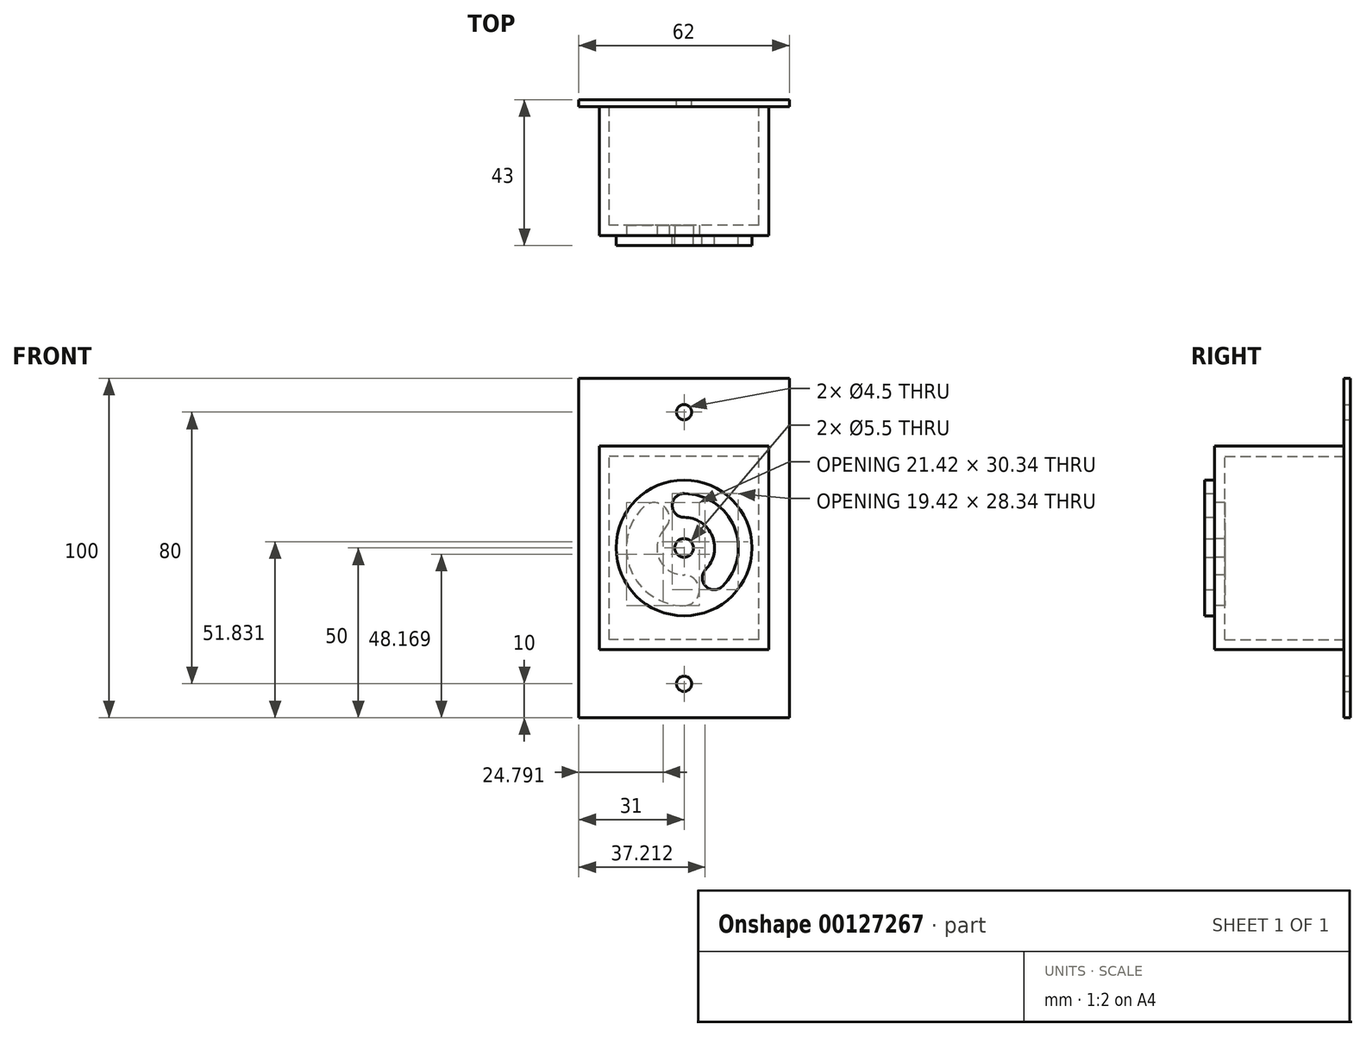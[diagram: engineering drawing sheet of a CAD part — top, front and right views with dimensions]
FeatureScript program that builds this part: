
annotation { "Feature Type Name" : "Feature", "Feature Type Description" : "" }
export const myFeature = defineFeature(function(context is Context, id is Id, definition is map)
    precondition{}
    {
        {
            var Q0;
            Q0=qCreatedBy(makeId("Front.planeOp"),FACE);
            var sketch = newSketch(context, id + "F0", { "sketchPlane" : qUnion([Q0])});
            skLineSegment(sketch, "E0.bottom", {"start": v(31, -50) * mm, "end": v(-31, -50) * mm});
            skLineSegment(sketch, "E0.top", {"start": v(31, 50) * mm, "end": v(-31, 50) * mm});
            skLineSegment(sketch, "E0.left", {"start": v(31, -50) * mm, "end": v(31, 50) * mm});
            skLineSegment(sketch, "E0.right", {"start": v(-31, -50) * mm, "end": v(-31, 50) * mm});
            skPoint(sketch, "E0.middle", {"position": v(0, 0) * mm});
            skCircle(sketch, "E1", {"center": v(0, 40) * mm, "radius": 2.25 * mm});
            skCircle(sketch, "E2.MirrorC", {"center": v(0, -40) * mm, "radius": 2.25 * mm});
            skSolve(sketch);
        }
        {
            var Q0;
            Q0=qSketchRegion(id+"F0",true);
            extrude(context, id + "F1", {"entities" : qUnion([Q0]), "depth" : 2 * mm});
        }
        {
            var Q0;
            Q0=makeQuery(id+"F1.opExtrude","CAP_FACE",FACE,{"disambiguationData":[OSD([sQuery(id+"F0.wireOp",EDGE,"E0.bottom"),sQuery(id+"F0.wireOp",EDGE,"E0.top"),sQuery(id+"F0.wireOp",EDGE,"E0.left"),sQuery(id+"F0.wireOp",EDGE,"E0.right"),sQuery(id+"F0.wireOp",EDGE,"E1"),sQuery(id+"F0.wireOp",EDGE,"E2.MirrorC")])],"isStart":false});
            var sketch = newSketch(context, id + "F2", { "sketchPlane" : qUnion([Q0])});
            skLineSegment(sketch, "E3.bottom", {"start": v(25, -30) * mm, "end": v(-25, -30) * mm});
            skLineSegment(sketch, "E3.top", {"start": v(25, 30) * mm, "end": v(-25, 30) * mm});
            skLineSegment(sketch, "E3.left", {"start": v(25, -30) * mm, "end": v(25, 30) * mm});
            skLineSegment(sketch, "E3.right", {"start": v(-25, -30) * mm, "end": v(-25, 30) * mm});
            skPoint(sketch, "E3.middle", {"position": v(0, 0) * mm});
            skLineSegment(sketch, "E4.0", {"start": v(-22, -27) * mm, "end": v(-22, 27) * mm});
            skLineSegment(sketch, "E4.1", {"start": v(22, -27) * mm, "end": v(-22, -27) * mm});
            skLineSegment(sketch, "E4.2", {"start": v(22, -27) * mm, "end": v(22, 27) * mm});
            skLineSegment(sketch, "E4.3", {"start": v(22, 27) * mm, "end": v(-22, 27) * mm});
            skSolve(sketch);
        }
        {
            var Q0;
            Q0=qSketchRegion(id+"F2",true);
            extrude(context, id + "F3", {"entities" : qUnion([Q0]), "operationType" : NewBodyOperationType.ADD, "depth" : 35 * mm});
        }
        {
            var Q0;
            Q0=makeQuery(id+"F3.boolean.opBoolean","SPLIT",FACE,{"disambiguationData":[TD([makeQuery(id+"F3.opExtrude","SWEPT_FACE",FACE,{"disambiguationData":[OSD([sQuery(id+"F2.wireOp",EDGE,"E4.0")])]})])],"derivedFrom":makeQuery(id+"F1.opExtrude","CAP_FACE",FACE,{"disambiguationData":[OSD([sQuery(id+"F0.wireOp",EDGE,"E0.bottom"),sQuery(id+"F0.wireOp",EDGE,"E0.top"),sQuery(id+"F0.wireOp",EDGE,"E0.left"),sQuery(id+"F0.wireOp",EDGE,"E0.right"),sQuery(id+"F0.wireOp",EDGE,"E1"),sQuery(id+"F0.wireOp",EDGE,"E2.MirrorC")])],"isStart":false})});
            extrude(context, id + "F4", {"entities" : qUnion([Q0]), "operationType" : NewBodyOperationType.REMOVE, "endBound" : BoundingType.THROUGH_ALL, "oppositeDirection" : true, "depth" : 25 * mm});
        }
        {
            var Q0;
            Q0=makeQuery(id+"F3.opExtrude","CAP_FACE",FACE,{"disambiguationData":[OSD([sQuery(id+"F2.wireOp",EDGE,"E3.bottom"),sQuery(id+"F2.wireOp",EDGE,"E3.top"),sQuery(id+"F2.wireOp",EDGE,"E3.left"),sQuery(id+"F2.wireOp",EDGE,"E3.right"),sQuery(id+"F2.wireOp",EDGE,"E4.0"),sQuery(id+"F2.wireOp",EDGE,"E4.1"),sQuery(id+"F2.wireOp",EDGE,"E4.2"),sQuery(id+"F2.wireOp",EDGE,"E4.3")])],"isStart":false});
            cPlane(context, id + "F5", {"entities" : qUnion([Q0]), "cplaneType" : CPlaneType.OFFSET, "offset" : 0 * mm, "width" : 150 * mm, "height" : 150 * mm});
        }
        {
            var Q0;
            Q0=qCreatedBy(id+"F5.planeOp",FACE);
            var sketch = newSketch(context, id + "F6", { "sketchPlane" : qUnion([Q0])});
            skLineSegment(sketch, "E5.0", {"start": v(25, 30) * mm, "end": v(-25, 30) * mm});
            skLineSegment(sketch, "E6.0", {"start": v(25, -30) * mm, "end": v(25, 30) * mm});
            skLineSegment(sketch, "E7.0", {"start": v(25, -30) * mm, "end": v(-25, -30) * mm});
            skLineSegment(sketch, "E8.0", {"start": v(-25, -30) * mm, "end": v(-25, 30) * mm});
            skSolve(sketch);
        }
        {
            var Q0;
            Q0=qSketchRegion(id+"F6",true);
            extrude(context, id + "F7", {"entities" : qUnion([Q0]), "operationType" : NewBodyOperationType.ADD, "depth" : 3 * mm});
        }
        {
            var Q0;
            Q0=makeQuery(id+"F7.opExtrude","CAP_FACE",FACE,{"disambiguationData":[OSD([sQuery(id+"F6.wireOp",EDGE,"E5.0"),sQuery(id+"F6.wireOp",EDGE,"E6.0"),sQuery(id+"F6.wireOp",EDGE,"E7.0"),sQuery(id+"F6.wireOp",EDGE,"E8.0")])],"isStart":false});
            var sketch = newSketch(context, id + "F8", { "sketchPlane" : qUnion([Q0])});
            skCircle(sketch, "E9", {"center": v(0, 0) * mm, "radius": 20 * mm});
            skLineSegment(sketch, "E10", {"start": v(-45.08, 0) * mm, "end": v(40.61, 0) * mm, "construction": true});
            skLineSegment(sketch, "E11", {"start": v(0, -55.26) * mm, "end": v(0, 12.5) * mm, "construction": true});
            skLineSegment(sketch, "E12", {"start": v(-42.64, -42.64) * mm, "end": v(42.64, 42.64) * mm, "construction": true});
            skLineSegment(sketch, "E13", {"start": v(-47.02, 47.02) * mm, "end": v(47.02, -47.02) * mm, "construction": true});
            skPoint(sketch, "E14", {"position": v(8.84, -8.84) * mm});
            skPoint(sketch, "E15", {"position": v(12.5, 0) * mm});
            skPoint(sketch, "E16", {"position": v(8.84, 8.84) * mm});
            skPoint(sketch, "E17", {"position": v(0, 12.5) * mm});
            skPoint(sketch, "E18", {"position": v(-8.84, 8.84) * mm});
            skPoint(sketch, "E19", {"position": v(-12.5, 0) * mm});
            skPoint(sketch, "E20", {"position": v(-8.84, -8.84) * mm});
            skPoint(sketch, "E21", {"position": v(0, -12.5) * mm});
            skArc(sketch, "E22", {"start": v(0, -12.5) * mm, "mid": v(4.78, -11.55) * mm, "end": v(8.84, -8.84) * mm});
            skArc(sketch, "E23", {"start": v(-8.84, 8.84) * mm, "mid": v(-11.55, -4.78) * mm, "end": v(0, -12.5) * mm});
            skLineSegment(sketch, "E24", {"start": v(0, 12.5) * mm, "end": v(0, 58.61) * mm, "construction": true});
            skArc(sketch, "E25", {"start": v(0, 12.5) * mm, "mid": v(-4.78, 11.55) * mm, "end": v(-8.84, 8.84) * mm});
            skArc(sketch, "E26", {"start": v(8.84, -8.84) * mm, "mid": v(11.55, 4.78) * mm, "end": v(0, 12.5) * mm});
            skCircle(sketch, "E27", {"center": v(0, 0) * mm, "radius": 2.75 * mm});
            skSolve(sketch);
        }
        {
            var Q0;
            Q0=makeQuery(id+"F7.opExtrude","CAP_FACE",FACE,{"disambiguationData":[OSD([sQuery(id+"F6.wireOp",EDGE,"E5.0"),sQuery(id+"F6.wireOp",EDGE,"E6.0"),sQuery(id+"F6.wireOp",EDGE,"E7.0"),sQuery(id+"F6.wireOp",EDGE,"E8.0")])],"isStart":false});
            cPlane(context, id + "F9", {"entities" : qUnion([Q0]), "cplaneType" : CPlaneType.OFFSET, "offset" : 0 * mm, "width" : 150 * mm, "height" : 150 * mm});
        }
        {
            var Q0;
            Q0=makeQuery(id+"F7.opExtrude","CAP_FACE",FACE,{"disambiguationData":[OSD([sQuery(id+"F6.wireOp",EDGE,"E5.0"),sQuery(id+"F6.wireOp",EDGE,"E6.0"),sQuery(id+"F6.wireOp",EDGE,"E7.0"),sQuery(id+"F6.wireOp",EDGE,"E8.0")])],"isStart":false});
            cPlane(context, id + "F10", {"entities" : qUnion([Q0]), "cplaneType" : CPlaneType.OFFSET, "offset" : 0 * mm, "width" : 150 * mm, "height" : 150 * mm});
        }
        {
            var Q0;
            Q0=makeQuery(id+"F8.imprint","IMPRINT",FACE,{"disambiguationData":[TD([[makeQuery(id+"F8.imprint","IMPRINT",EDGE,{"derivedFrom":sQuery(id+"F8.wireOp",EDGE,"E9")}),1.0]])]});
            var Q1;
            Q1=makeQuery(id+"F8.imprint","IMPRINT",FACE,{"disambiguationData":[TD([[makeQuery(id+"F8.imprint","IMPRINT",EDGE,{"derivedFrom":sQuery(id+"F8.wireOp",EDGE,"E22")}),1.0]])]});
            var Q2;
            Q2=sQuery(id+"F8.wireOp",EDGE,"E9");
            extrude(context, id + "F11", {"entities" : qUnion([Q0, Q1]), "surfaceEntities" : qUnion([Q2]), "depth" : 3 * mm});
        }
        {
            var Q0;
            Q0=qCreatedBy(id+"F9.planeOp",FACE);
            var sketch = newSketch(context, id + "F12", { "sketchPlane" : qUnion([Q0])});
            skArc(sketch, "E28.0", {"start": v(-8.84, 8.84) * mm, "mid": v(-11.55, -4.78) * mm, "end": v(0, -12.5) * mm});
            skArc(sketch, "E29.0.startCap", {"start": v(-12.02, 12.02) * mm, "mid": v(-5.66, 12.02) * mm, "end": v(-5.66, 5.66) * mm});
            skArc(sketch, "E29.0.endCap", {"start": v(0, -8) * mm, "mid": v(4.5, -12.5) * mm, "end": v(0, -17) * mm});
            skArc(sketch, "E29.0.left", {"start": v(-5.66, 5.66) * mm, "mid": v(-7.4, -3.06) * mm, "end": v(0, -8) * mm});
            skArc(sketch, "E29.0.right", {"start": v(-12.02, 12.02) * mm, "mid": v(-15.7, -6.5) * mm, "end": v(0, -17) * mm});
            skSolve(sketch);
        }
        {
            var Q0;
            Q0=qCreatedBy(id+"F10.planeOp",FACE);
            var sketch = newSketch(context, id + "F13", { "sketchPlane" : qUnion([Q0])});
            skArc(sketch, "E30.0", {"start": v(8.84, -8.84) * mm, "mid": v(11.55, 4.78) * mm, "end": v(0, 12.5) * mm});
            skArc(sketch, "E31.0.startCap", {"start": v(11.31, -11.31) * mm, "mid": v(6.36, -11.31) * mm, "end": v(6.36, -6.36) * mm});
            skArc(sketch, "E31.0.endCap", {"start": v(0, 9) * mm, "mid": v(-3.5, 12.5) * mm, "end": v(0, 16) * mm});
            skArc(sketch, "E31.0.left", {"start": v(6.36, -6.36) * mm, "mid": v(8.31, 3.44) * mm, "end": v(0, 9) * mm});
            skArc(sketch, "E31.0.right", {"start": v(11.31, -11.31) * mm, "mid": v(14.78, 6.12) * mm, "end": v(0, 16) * mm});
            skSolve(sketch);
        }
        {
            var Q0;
            Q0=qSketchRegion(id+"F13",true);
            extrude(context, id + "F14", {"entities" : qUnion([Q0]), "operationType" : NewBodyOperationType.REMOVE, "endBound" : BoundingType.THROUGH_ALL, "depth" : 25 * mm});
        }
        {
            var Q0;
            Q0=qSketchRegion(id+"F12",true);
            extrude(context, id + "F15", {"entities" : qUnion([Q0]), "operationType" : NewBodyOperationType.REMOVE, "endBound" : BoundingType.THROUGH_ALL, "oppositeDirection" : true, "depth" : 25 * mm});
        }
        {
            var Q0;
            Q0=makeQuery(id+"F8.imprint","IMPRINT",FACE,{"disambiguationData":[TD([[makeQuery(id+"F8.imprint","IMPRINT",EDGE,{"derivedFrom":sQuery(id+"F8.wireOp",EDGE,"E27")}),1.0]])]});
            var Q1;
            Q1=sQuery(id+"F8.wireOp",EDGE,"E27");
            extrude(context, id + "F16", {"entities" : qUnion([Q0]), "operationType" : NewBodyOperationType.REMOVE, "surfaceEntities" : qUnion([Q1]), "endBound" : BoundingType.THROUGH_ALL, "oppositeDirection" : true, "depth" : 25 * mm});
        }
    });
